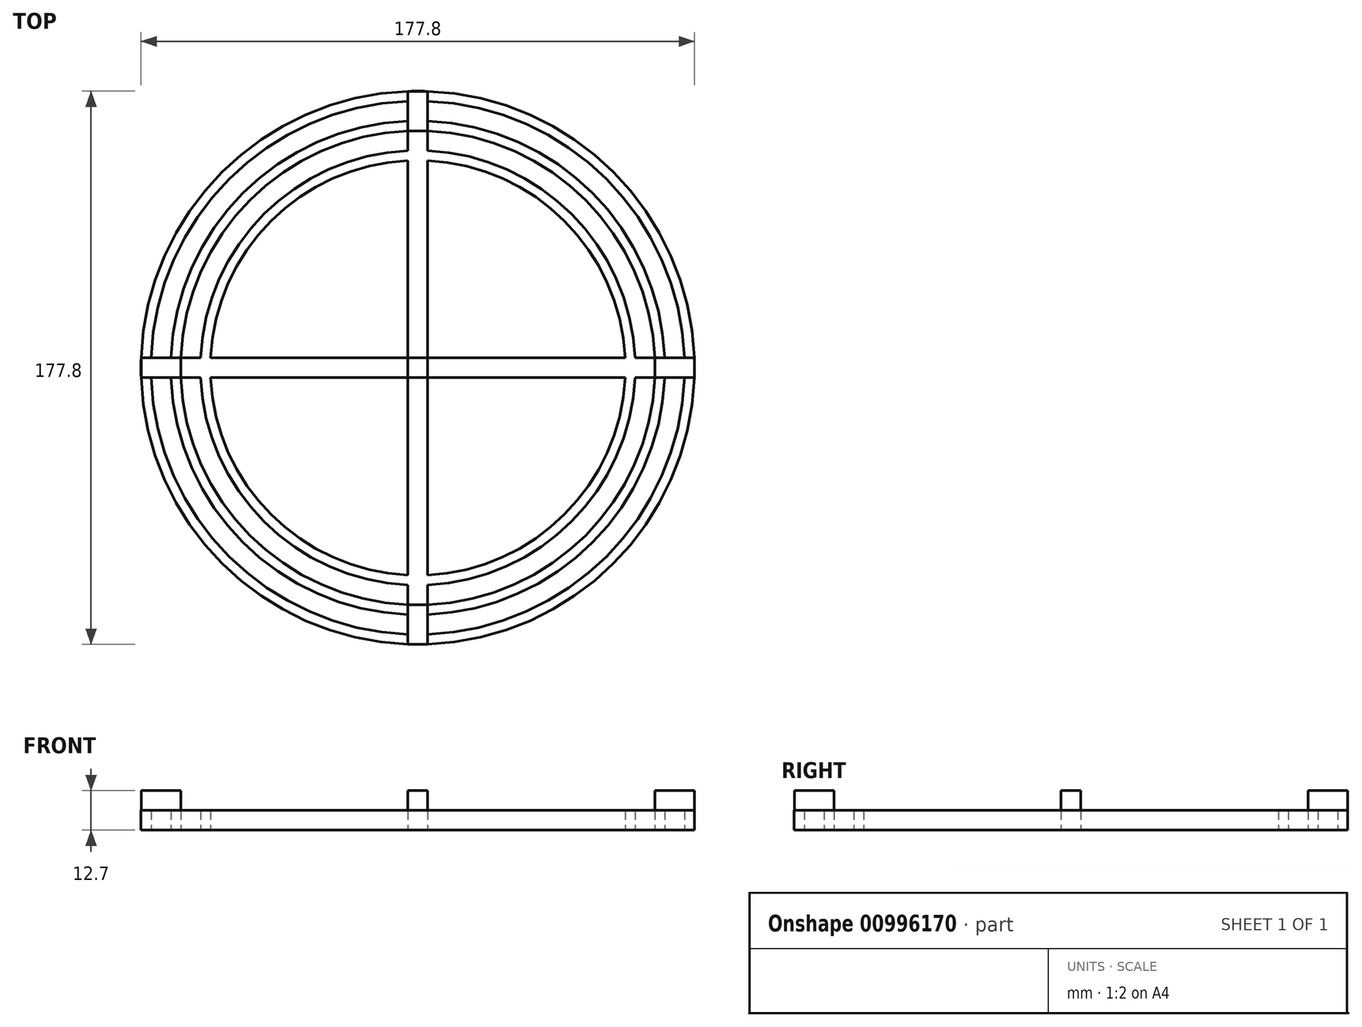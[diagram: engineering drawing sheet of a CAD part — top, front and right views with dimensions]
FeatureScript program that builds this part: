
annotation { "Feature Type Name" : "Feature", "Feature Type Description" : "" }
export const myFeature = defineFeature(function(context is Context, id is Id, definition is map)
    precondition{}
    {
        {
            var Q0;
            Q0=qCreatedBy(makeId("Top.planeOp"),FACE);
            var sketch = newSketch(context, id + "F0", { "sketchPlane" : qUnion([Q0])});
            skCircle(sketch, "E0", {"center": v(0, 0) * mm, "radius": 88.9 * mm});
            skCircle(sketch, "E1", {"center": v(0, 0) * mm, "radius": 85.73 * mm});
            skCircle(sketch, "E2", {"center": v(0, 0) * mm, "radius": 79.38 * mm});
            skCircle(sketch, "E3", {"center": v(0, 0) * mm, "radius": 76.2 * mm});
            skCircle(sketch, "E4", {"center": v(0, 0) * mm, "radius": 69.85 * mm});
            skCircle(sketch, "E5", {"center": v(0, 0) * mm, "radius": 66.68 * mm});
            skLineSegment(sketch, "E6.bottom", {"start": v(3.18, -88.84) * mm, "end": v(-3.17, -88.84) * mm});
            skLineSegment(sketch, "E6.top", {"start": v(3.17, 88.84) * mm, "end": v(-3.18, 88.84) * mm});
            skLineSegment(sketch, "E6.left", {"start": v(3.18, -88.84) * mm, "end": v(3.17, 88.84) * mm});
            skLineSegment(sketch, "E6.right", {"start": v(-3.17, -88.84) * mm, "end": v(-3.18, 88.84) * mm});
            skLineSegment(sketch, "E7.bottom", {"start": v(88.84, -3.18) * mm, "end": v(-88.84, -3.18) * mm});
            skLineSegment(sketch, "E7.top", {"start": v(88.84, 3.18) * mm, "end": v(-88.84, 3.17) * mm});
            skLineSegment(sketch, "E7.left", {"start": v(88.84, -3.18) * mm, "end": v(88.84, 3.18) * mm});
            skLineSegment(sketch, "E7.right", {"start": v(-88.84, -3.18) * mm, "end": v(-88.84, 3.18) * mm});
            skSolve(sketch);
        }
        {
            var Q0;
            Q0 = qSketchRegion(id + "F0", true);
            var Q1;
            {var subQ0=sQuery(id+"F0.wireOp",EDGE,"E6.right");var subQ1=sQuery(id+"F0.wireOp",EDGE,"E2");var subQ2=makeQuery(id+"F0.imprint","INTERSECT",VERTEX,{"disambiguationData":[OD(0.0)],"derivedFrom":[subQ1,subQ0]});Q1=makeQuery(id+"F0.imprint","IMPRINT",FACE,{"disambiguationData":[TD([[makeQuery(id+"F0.imprint","IMPRINT",EDGE,{"disambiguationData":[TD([[subQ2,-1.0]])],"derivedFrom":subQ1}),1.0]])]});}
            var Q2;
            {var subQ0=sQuery(id+"F0.wireOp",EDGE,"E7.bottom");var subQ1=sQuery(id+"F0.wireOp",EDGE,"E2");var subQ2=makeQuery(id+"F0.imprint","INTERSECT",VERTEX,{"disambiguationData":[OD(0.0)],"derivedFrom":[subQ1,subQ0]});Q2=makeQuery(id+"F0.imprint","IMPRINT",FACE,{"disambiguationData":[TD([[makeQuery(id+"F0.imprint","IMPRINT",EDGE,{"disambiguationData":[TD([[subQ2,-1.0]])],"derivedFrom":subQ1}),1.0]])]});}
            var Q3;
            {var subQ0=sQuery(id+"F0.wireOp",EDGE,"E7.top");var subQ1=sQuery(id+"F0.wireOp",EDGE,"E2");var subQ2=makeQuery(id+"F0.imprint","INTERSECT",VERTEX,{"disambiguationData":[OD(1.0)],"derivedFrom":[subQ1,subQ0]});Q3=makeQuery(id+"F0.imprint","IMPRINT",FACE,{"disambiguationData":[TD([[makeQuery(id+"F0.imprint","IMPRINT",EDGE,{"disambiguationData":[TD([[subQ2,-1.0]])],"derivedFrom":subQ1}),1.0]])]});}
            var Q4;
            {var subQ0=sQuery(id+"F0.wireOp",EDGE,"E7.top");var subQ1=sQuery(id+"F0.wireOp",EDGE,"E1");var subQ2=makeQuery(id+"F0.imprint","INTERSECT",VERTEX,{"disambiguationData":[OD(1.0)],"derivedFrom":[subQ1,subQ0]});Q4=makeQuery(id+"F0.imprint","IMPRINT",FACE,{"disambiguationData":[TD([[makeQuery(id+"F0.imprint","IMPRINT",EDGE,{"disambiguationData":[TD([[subQ2,-1.0]])],"derivedFrom":subQ1}),1.0]])]});}
            var Q5;
            {var subQ0=sQuery(id+"F0.wireOp",EDGE,"E7.top");var subQ1=sQuery(id+"F0.wireOp",EDGE,"E4");var subQ2=makeQuery(id+"F0.imprint","INTERSECT",VERTEX,{"disambiguationData":[OD(1.0)],"derivedFrom":[subQ1,subQ0]});Q5=makeQuery(id+"F0.imprint","IMPRINT",FACE,{"disambiguationData":[TD([[makeQuery(id+"F0.imprint","IMPRINT",EDGE,{"disambiguationData":[TD([[subQ2,-1.0]])],"derivedFrom":subQ1}),1.0]])]});}
            var Q6;
            {var subQ0=sQuery(id+"F0.wireOp",EDGE,"E6.right");var subQ1=sQuery(id+"F0.wireOp",EDGE,"E4");var subQ2=makeQuery(id+"F0.imprint","INTERSECT",VERTEX,{"disambiguationData":[OD(0.0)],"derivedFrom":[subQ1,subQ0]});Q6=makeQuery(id+"F0.imprint","IMPRINT",FACE,{"disambiguationData":[TD([[makeQuery(id+"F0.imprint","IMPRINT",EDGE,{"disambiguationData":[TD([[subQ2,-1.0]])],"derivedFrom":subQ1}),1.0]])]});}
            var Q7;
            {var subQ0=sQuery(id+"F0.wireOp",EDGE,"E7.bottom");var subQ1=sQuery(id+"F0.wireOp",EDGE,"E4");var subQ2=makeQuery(id+"F0.imprint","INTERSECT",VERTEX,{"disambiguationData":[OD(0.0)],"derivedFrom":[subQ1,subQ0]});Q7=makeQuery(id+"F0.imprint","IMPRINT",FACE,{"disambiguationData":[TD([[makeQuery(id+"F0.imprint","IMPRINT",EDGE,{"disambiguationData":[TD([[subQ2,-1.0]])],"derivedFrom":subQ1}),1.0]])]});}
            var Q8;
            {var subQ0=sQuery(id+"F0.wireOp",EDGE,"E6.right");var subQ1=sQuery(id+"F0.wireOp",EDGE,"E4");var subQ2=makeQuery(id+"F0.imprint","INTERSECT",VERTEX,{"disambiguationData":[OD(1.0)],"derivedFrom":[subQ1,subQ0]});Q8=makeQuery(id+"F0.imprint","IMPRINT",FACE,{"disambiguationData":[TD([[makeQuery(id+"F0.imprint","IMPRINT",EDGE,{"disambiguationData":[TD([[subQ2,-1.0]])],"derivedFrom":subQ1}),1.0]])]});}
            var Q9;
            {var subQ0=sQuery(id+"F0.wireOp",EDGE,"E6.right");var subQ1=sQuery(id+"F0.wireOp",EDGE,"E2");var subQ2=makeQuery(id+"F0.imprint","INTERSECT",VERTEX,{"disambiguationData":[OD(1.0)],"derivedFrom":[subQ1,subQ0]});Q9=makeQuery(id+"F0.imprint","IMPRINT",FACE,{"disambiguationData":[TD([[makeQuery(id+"F0.imprint","IMPRINT",EDGE,{"disambiguationData":[TD([[subQ2,-1.0]])],"derivedFrom":subQ1}),1.0]])]});}
            var Q10;
            {var subQ0=sQuery(id+"F0.wireOp",EDGE,"E6.left");var subQ1=sQuery(id+"F0.wireOp",EDGE,"E2");var subQ2=makeQuery(id+"F0.imprint","INTERSECT",VERTEX,{"disambiguationData":[OD(1.0)],"derivedFrom":[subQ1,subQ0]});Q10=makeQuery(id+"F0.imprint","IMPRINT",FACE,{"disambiguationData":[TD([[makeQuery(id+"F0.imprint","IMPRINT",EDGE,{"disambiguationData":[TD([[subQ2,-1.0]])],"derivedFrom":subQ1}),1.0]])]});}
            var Q11;
            {var subQ0=sQuery(id+"F0.wireOp",EDGE,"E6.left");var subQ1=sQuery(id+"F0.wireOp",EDGE,"E4");var subQ2=makeQuery(id+"F0.imprint","INTERSECT",VERTEX,{"disambiguationData":[OD(1.0)],"derivedFrom":[subQ1,subQ0]});Q11=makeQuery(id+"F0.imprint","IMPRINT",FACE,{"disambiguationData":[TD([[makeQuery(id+"F0.imprint","IMPRINT",EDGE,{"disambiguationData":[TD([[subQ2,-1.0]])],"derivedFrom":subQ1}),1.0]])]});}
            var Q12;
            {var subQ0=sQuery(id+"F0.wireOp",EDGE,"E7.top");var subQ1=sQuery(id+"F0.wireOp",EDGE,"E4");var subQ2=makeQuery(id+"F0.imprint","INTERSECT",VERTEX,{"disambiguationData":[OD(0.0)],"derivedFrom":[subQ1,subQ0]});Q12=makeQuery(id+"F0.imprint","IMPRINT",FACE,{"disambiguationData":[TD([[makeQuery(id+"F0.imprint","IMPRINT",EDGE,{"disambiguationData":[TD([[subQ2,1.0]])],"derivedFrom":subQ1}),1.0]])]});}
            var Q13;
            {var subQ0=sQuery(id+"F0.wireOp",EDGE,"E6.left");var subQ1=sQuery(id+"F0.wireOp",EDGE,"E2");var subQ2=makeQuery(id+"F0.imprint","INTERSECT",VERTEX,{"disambiguationData":[OD(0.0)],"derivedFrom":[subQ1,subQ0]});Q13=makeQuery(id+"F0.imprint","IMPRINT",FACE,{"disambiguationData":[TD([[makeQuery(id+"F0.imprint","IMPRINT",EDGE,{"disambiguationData":[TD([[subQ2,1.0]])],"derivedFrom":subQ1}),1.0]])]});}
            var Q14;
            {var subQ0=sQuery(id+"F0.wireOp",EDGE,"E6.left");var subQ1=sQuery(id+"F0.wireOp",EDGE,"E4");var subQ2=makeQuery(id+"F0.imprint","INTERSECT",VERTEX,{"disambiguationData":[OD(0.0)],"derivedFrom":[subQ1,subQ0]});Q14=makeQuery(id+"F0.imprint","IMPRINT",FACE,{"disambiguationData":[TD([[makeQuery(id+"F0.imprint","IMPRINT",EDGE,{"disambiguationData":[TD([[subQ2,1.0]])],"derivedFrom":subQ1}),1.0]])]});}
            var Q15;
            {var subQ0=sQuery(id+"F0.wireOp",EDGE,"E6.left");var subQ1=sQuery(id+"F0.wireOp",EDGE,"E2");var subQ2=makeQuery(id+"F0.imprint","INTERSECT",VERTEX,{"disambiguationData":[OD(0.0)],"derivedFrom":[subQ1,subQ0]});Q15=makeQuery(id+"F0.imprint","IMPRINT",FACE,{"disambiguationData":[TD([[makeQuery(id+"F0.imprint","IMPRINT",EDGE,{"disambiguationData":[TD([[subQ2,-1.0]])],"derivedFrom":subQ1}),1.0]])]});}
            var Q16;
            {var subQ0=sQuery(id+"F0.wireOp",EDGE,"E6.left");var subQ1=sQuery(id+"F0.wireOp",EDGE,"E4");var subQ2=makeQuery(id+"F0.imprint","INTERSECT",VERTEX,{"disambiguationData":[OD(0.0)],"derivedFrom":[subQ1,subQ0]});Q16=makeQuery(id+"F0.imprint","IMPRINT",FACE,{"disambiguationData":[TD([[makeQuery(id+"F0.imprint","IMPRINT",EDGE,{"disambiguationData":[TD([[subQ2,-1.0]])],"derivedFrom":subQ1}),1.0]])]});}
            var Q17;
            {var subQ0=sQuery(id+"F0.wireOp",EDGE,"E7.top");var subQ1=sQuery(id+"F0.wireOp",EDGE,"E5");var subQ2=makeQuery(id+"F0.imprint","INTERSECT",VERTEX,{"disambiguationData":[OD(1.0)],"derivedFrom":[subQ1,subQ0]});Q17=makeQuery(id+"F0.imprint","IMPRINT",FACE,{"disambiguationData":[TD([[makeQuery(id+"F0.imprint","IMPRINT",EDGE,{"disambiguationData":[TD([[subQ2,-1.0]])],"derivedFrom":subQ1}),1.0]])]});}
            var Q18;
            {var subQ0=sQuery(id+"F0.wireOp",EDGE,"E6.left");var subQ1=sQuery(id+"F0.wireOp",EDGE,"E5");var subQ2=makeQuery(id+"F0.imprint","INTERSECT",VERTEX,{"disambiguationData":[OD(0.0)],"derivedFrom":[subQ1,subQ0]});Q18=makeQuery(id+"F0.imprint","IMPRINT",FACE,{"disambiguationData":[TD([[makeQuery(id+"F0.imprint","IMPRINT",EDGE,{"disambiguationData":[TD([[subQ2,-1.0]])],"derivedFrom":subQ1}),1.0]])]});}
            var Q19;
            {var subQ0=sQuery(id+"F0.wireOp",EDGE,"E7.top");var subQ1=sQuery(id+"F0.wireOp",EDGE,"E5");var subQ2=makeQuery(id+"F0.imprint","INTERSECT",VERTEX,{"disambiguationData":[OD(0.0)],"derivedFrom":[subQ1,subQ0]});Q19=makeQuery(id+"F0.imprint","IMPRINT",FACE,{"disambiguationData":[TD([[makeQuery(id+"F0.imprint","IMPRINT",EDGE,{"disambiguationData":[TD([[subQ2,1.0]])],"derivedFrom":subQ1}),1.0]])]});}
            var Q20;
            {var subQ0=sQuery(id+"F0.wireOp",EDGE,"E6.right");var subQ1=sQuery(id+"F0.wireOp",EDGE,"E5");var subQ2=makeQuery(id+"F0.imprint","INTERSECT",VERTEX,{"disambiguationData":[OD(1.0)],"derivedFrom":[subQ1,subQ0]});Q20=makeQuery(id+"F0.imprint","IMPRINT",FACE,{"disambiguationData":[TD([[makeQuery(id+"F0.imprint","IMPRINT",EDGE,{"disambiguationData":[TD([[subQ2,-1.0]])],"derivedFrom":subQ1}),1.0]])]});}
            var Q21;
            {var subQ0=sQuery(id+"F0.wireOp",EDGE,"E7.bottom");var subQ1=sQuery(id+"F0.wireOp",EDGE,"E6.left");var subQ2=makeQuery(id+"F0.imprint","INTERSECT",VERTEX,{"derivedFrom":[subQ1,subQ0]});Q21=makeQuery(id+"F0.imprint","IMPRINT",FACE,{"disambiguationData":[TD([[makeQuery(id+"F0.imprint","IMPRINT",EDGE,{"disambiguationData":[TD([[subQ2,-1.0]])],"derivedFrom":subQ1}),1.0]])]});}
            var Q22;
            {var subQ0=sQuery(id+"F0.wireOp",EDGE,"E6.right");var subQ1=sQuery(id+"F0.wireOp",EDGE,"E3");var subQ2=makeQuery(id+"F0.imprint","INTERSECT",VERTEX,{"disambiguationData":[OD(1.0)],"derivedFrom":[subQ1,subQ0]});Q22=makeQuery(id+"F0.imprint","IMPRINT",FACE,{"disambiguationData":[TD([[makeQuery(id+"F0.imprint","IMPRINT",EDGE,{"disambiguationData":[TD([[subQ2,-1.0]])],"derivedFrom":subQ1}),1.0]])]});}
            var Q23;
            {var subQ0=sQuery(id+"F0.wireOp",EDGE,"E6.right");var subQ1=sQuery(id+"F0.wireOp",EDGE,"E1");var subQ2=makeQuery(id+"F0.imprint","INTERSECT",VERTEX,{"disambiguationData":[OD(1.0)],"derivedFrom":[subQ1,subQ0]});Q23=makeQuery(id+"F0.imprint","IMPRINT",FACE,{"disambiguationData":[TD([[makeQuery(id+"F0.imprint","IMPRINT",EDGE,{"disambiguationData":[TD([[subQ2,-1.0]])],"derivedFrom":subQ1}),1.0]])]});}
            var Q24;
            {var subQ0=sQuery(id+"F0.wireOp",EDGE,"E6.left");var subQ1=sQuery(id+"F0.wireOp",EDGE,"E3");var subQ2=makeQuery(id+"F0.imprint","INTERSECT",VERTEX,{"disambiguationData":[OD(0.0)],"derivedFrom":[subQ1,subQ0]});Q24=makeQuery(id+"F0.imprint","IMPRINT",FACE,{"disambiguationData":[TD([[makeQuery(id+"F0.imprint","IMPRINT",EDGE,{"disambiguationData":[TD([[subQ2,-1.0]])],"derivedFrom":subQ1}),1.0]])]});}
            var Q25;
            {var subQ0=sQuery(id+"F0.wireOp",EDGE,"E6.left");var subQ1=sQuery(id+"F0.wireOp",EDGE,"E1");var subQ2=makeQuery(id+"F0.imprint","INTERSECT",VERTEX,{"disambiguationData":[OD(0.0)],"derivedFrom":[subQ1,subQ0]});Q25=makeQuery(id+"F0.imprint","IMPRINT",FACE,{"disambiguationData":[TD([[makeQuery(id+"F0.imprint","IMPRINT",EDGE,{"disambiguationData":[TD([[subQ2,-1.0]])],"derivedFrom":subQ1}),1.0]])]});}
            var Q26;
            {var subQ0=sQuery(id+"F0.wireOp",EDGE,"E7.top");var subQ1=sQuery(id+"F0.wireOp",EDGE,"E3");var subQ2=makeQuery(id+"F0.imprint","INTERSECT",VERTEX,{"disambiguationData":[OD(1.0)],"derivedFrom":[subQ1,subQ0]});Q26=makeQuery(id+"F0.imprint","IMPRINT",FACE,{"disambiguationData":[TD([[makeQuery(id+"F0.imprint","IMPRINT",EDGE,{"disambiguationData":[TD([[subQ2,-1.0]])],"derivedFrom":subQ1}),1.0]])]});}
            var Q27;
            {var subQ0=sQuery(id+"F0.wireOp",EDGE,"E7.top");var subQ1=sQuery(id+"F0.wireOp",EDGE,"E3");var subQ2=makeQuery(id+"F0.imprint","INTERSECT",VERTEX,{"disambiguationData":[OD(0.0)],"derivedFrom":[subQ1,subQ0]});Q27=makeQuery(id+"F0.imprint","IMPRINT",FACE,{"disambiguationData":[TD([[makeQuery(id+"F0.imprint","IMPRINT",EDGE,{"disambiguationData":[TD([[subQ2,1.0]])],"derivedFrom":subQ1}),1.0]])]});}
            var Q28;
            {var subQ0=sQuery(id+"F0.wireOp",EDGE,"E7.top");var subQ1=sQuery(id+"F0.wireOp",EDGE,"E2");var subQ2=makeQuery(id+"F0.imprint","INTERSECT",VERTEX,{"disambiguationData":[OD(0.0)],"derivedFrom":[subQ1,subQ0]});Q28=makeQuery(id+"F0.imprint","IMPRINT",FACE,{"disambiguationData":[TD([[makeQuery(id+"F0.imprint","IMPRINT",EDGE,{"disambiguationData":[TD([[subQ2,1.0]])],"derivedFrom":subQ1}),1.0]])]});}
            var Q29;
            {var subQ0=sQuery(id+"F0.wireOp",EDGE,"E7.top");var subQ1=sQuery(id+"F0.wireOp",EDGE,"E1");var subQ2=makeQuery(id+"F0.imprint","INTERSECT",VERTEX,{"disambiguationData":[OD(0.0)],"derivedFrom":[subQ1,subQ0]});Q29=makeQuery(id+"F0.imprint","IMPRINT",FACE,{"disambiguationData":[TD([[makeQuery(id+"F0.imprint","IMPRINT",EDGE,{"disambiguationData":[TD([[subQ2,1.0]])],"derivedFrom":subQ1}),1.0]])]});}
            extrude(context, id + "F1", {"entities" : qUnion([Q0, Q1, Q2, Q3, Q4, Q5, Q6, Q7, Q8, Q9, Q10, Q11, Q12, Q13, Q14, Q15, Q16, Q17, Q18, Q19, Q20, Q21, Q22, Q23, Q24, Q25, Q26, Q27, Q28, Q29]), "depth" : 6.35 * mm, "offsetDistance" : 25.4 * mm});
        }
        {
            var Q0;
            Q0=makeQuery(id+"F1.opExtrude","CAP_FACE",FACE,{"disambiguationData":[OSD([sQuery(id+"F0.wireOp",EDGE,"E0"),sQuery(id+"F0.wireOp",EDGE,"E1"),sQuery(id+"F0.wireOp",EDGE,"E2"),sQuery(id+"F0.wireOp",EDGE,"E3"),sQuery(id+"F0.wireOp",EDGE,"E4"),sQuery(id+"F0.wireOp",EDGE,"E5"),sQuery(id+"F0.wireOp",EDGE,"E6.left"),sQuery(id+"F0.wireOp",EDGE,"E6.right"),sQuery(id+"F0.wireOp",EDGE,"E7.bottom"),sQuery(id+"F0.wireOp",EDGE,"E7.top")])],"isStart":false});
            var sketch = newSketch(context, id + "F2", { "sketchPlane" : qUnion([Q0])});
            skLineSegment(sketch, "E8.bottom", {"start": v(-76.13, 3.17) * mm, "end": v(-88.84, 3.17) * mm});
            skLineSegment(sketch, "E8.top", {"start": v(-76.13, -3.17) * mm, "end": v(-88.84, -3.17) * mm});
            skLineSegment(sketch, "E8.left", {"start": v(-76.13, 3.17) * mm, "end": v(-76.13, -3.17) * mm});
            skLineSegment(sketch, "E8.right", {"start": v(-88.84, 3.17) * mm, "end": v(-88.84, -3.17) * mm});
            skLineSegment(sketch, "E9.bottom", {"start": v(76.13, 3.18) * mm, "end": v(88.84, 3.18) * mm});
            skLineSegment(sketch, "E9.top", {"start": v(76.13, -3.18) * mm, "end": v(88.84, -3.18) * mm});
            skLineSegment(sketch, "E9.left", {"start": v(76.13, 3.18) * mm, "end": v(76.13, -3.18) * mm});
            skLineSegment(sketch, "E9.right", {"start": v(88.84, 3.18) * mm, "end": v(88.84, -3.18) * mm});
            skLineSegment(sketch, "E10.bottom", {"start": v(3.17, 76.13) * mm, "end": v(-3.18, 76.13) * mm});
            skLineSegment(sketch, "E10.top", {"start": v(3.17, 88.84) * mm, "end": v(-3.18, 88.84) * mm});
            skLineSegment(sketch, "E10.left", {"start": v(3.17, 76.13) * mm, "end": v(3.17, 88.84) * mm});
            skLineSegment(sketch, "E10.right", {"start": v(-3.18, 76.13) * mm, "end": v(-3.18, 88.84) * mm});
            skLineSegment(sketch, "E11.bottom", {"start": v(-3.17, -76.13) * mm, "end": v(3.18, -76.13) * mm});
            skLineSegment(sketch, "E11.top", {"start": v(-3.17, -88.84) * mm, "end": v(3.18, -88.84) * mm});
            skLineSegment(sketch, "E11.left", {"start": v(-3.17, -76.13) * mm, "end": v(-3.17, -88.84) * mm});
            skLineSegment(sketch, "E11.right", {"start": v(3.18, -76.13) * mm, "end": v(3.18, -88.84) * mm});
            skLineSegment(sketch, "E12.bottom", {"start": v(-3.18, -3.18) * mm, "end": v(3.18, -3.18) * mm});
            skLineSegment(sketch, "E12.top", {"start": v(-3.18, 3.18) * mm, "end": v(3.18, 3.18) * mm});
            skLineSegment(sketch, "E12.left", {"start": v(-3.18, -3.18) * mm, "end": v(-3.18, 3.18) * mm});
            skLineSegment(sketch, "E12.right", {"start": v(3.18, -3.18) * mm, "end": v(3.18, 3.18) * mm});
            skSolve(sketch);
        }
        {
            var Q0;
            Q0 = qSketchRegion(id + "F2", true);
            extrude(context, id + "F3", {"entities" : qUnion([Q0]), "operationType" : NewBodyOperationType.ADD, "depth" : 6.35 * mm, "offsetDistance" : 25.4 * mm});
        }
    });
